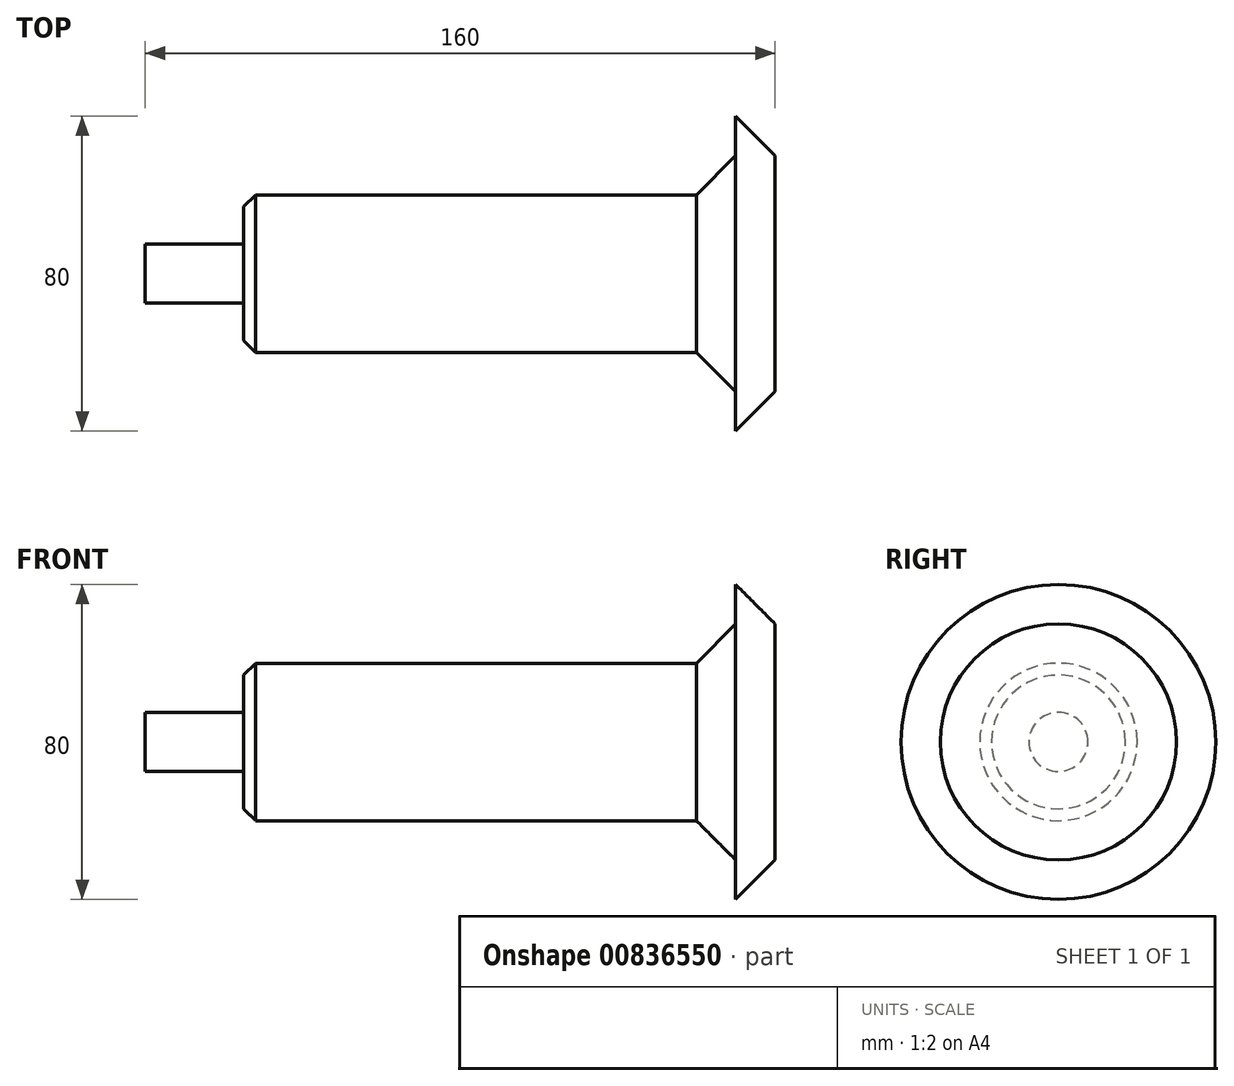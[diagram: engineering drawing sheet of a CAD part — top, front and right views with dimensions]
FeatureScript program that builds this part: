
annotation { "Feature Type Name" : "Feature", "Feature Type Description" : "" }
export const myFeature = defineFeature(function(context is Context, id is Id, definition is map)
    precondition{}
    {
        {
            var Q0;
            Q0=qCreatedBy(makeId("Top.planeOp"),FACE);
            var sketch = newSketch(context, id + "F0", { "sketchPlane" : qUnion([Q0])});
            skLineSegment(sketch, "E0", {"start": v(80, 0) * mm, "end": v(-80, 0) * mm});
            skLineSegment(sketch, "E1", {"start": v(-80, 0) * mm, "end": v(-80, 7.5) * mm});
            skLineSegment(sketch, "E2", {"start": v(-80, 7.5) * mm, "end": v(-55, 7.5) * mm});
            skLineSegment(sketch, "E3", {"start": v(-55, 7.5) * mm, "end": v(-55, 20) * mm});
            skLineSegment(sketch, "E4", {"start": v(-55, 20) * mm, "end": v(70, 20) * mm});
            skLineSegment(sketch, "E5", {"start": v(70, 20) * mm, "end": v(70, 40) * mm});
            skLineSegment(sketch, "E6", {"start": v(70, 40) * mm, "end": v(80, 40) * mm});
            skLineSegment(sketch, "E7", {"start": v(80, 40) * mm, "end": v(80, 0) * mm});
            skSolve(sketch);
        }
        {
            var Q0;
            Q0=makeQuery(id+"F0.imprint","IMPRINT",FACE,{"disambiguationData":[TD([[makeQuery(id+"F0.imprint","IMPRINT",EDGE,{"derivedFrom":sQuery(id+"F0.wireOp",EDGE,"E0")}),-1.0]])]});
            var Q1;
            Q1=sQuery(id+"F0.wireOp",EDGE,"E0");
            revolve(context, id + "F1", {"surfaceOperationType" : NewSurfaceOperationType.NEW, "entities" : qUnion([Q0]), "axis" : qUnion([Q1]), "revolveType" : RevolveType.FULL});
        }
        {
            var Q0;
            Q0=makeQuery(id+"F1.opRevolve","SWEPT_EDGE",EDGE,{"disambiguationData":[OSD([sQuery(id+"F0.wireOp",EDGE,"E3"),sQuery(id+"F0.wireOp",EDGE,"E4")])]});
            chamfer(context, id + "F2", {"entities" : qUnion([Q0]), "width" : 3 * mm, "tangentPropagation" : true});
        }
        {
            var Q0;
            Q0=makeQuery(id+"F1.opRevolve","SWEPT_EDGE",EDGE,{"disambiguationData":[OSD([sQuery(id+"F0.wireOp",EDGE,"E4"),sQuery(id+"F0.wireOp",EDGE,"E5")])]});
            chamfer(context, id + "F3", {"entities" : qUnion([Q0]), "width" : 10 * mm, "tangentPropagation" : true});
        }
        {
            var Q0;
            Q0=makeQuery(id+"F1.opRevolve","SWEPT_EDGE",EDGE,{"disambiguationData":[OSD([sQuery(id+"F0.wireOp",EDGE,"E6"),sQuery(id+"F0.wireOp",EDGE,"E7")])]});
            chamfer(context, id + "F4", {"entities" : qUnion([Q0]), "width" : 10 * mm, "tangentPropagation" : true});
        }
    });
